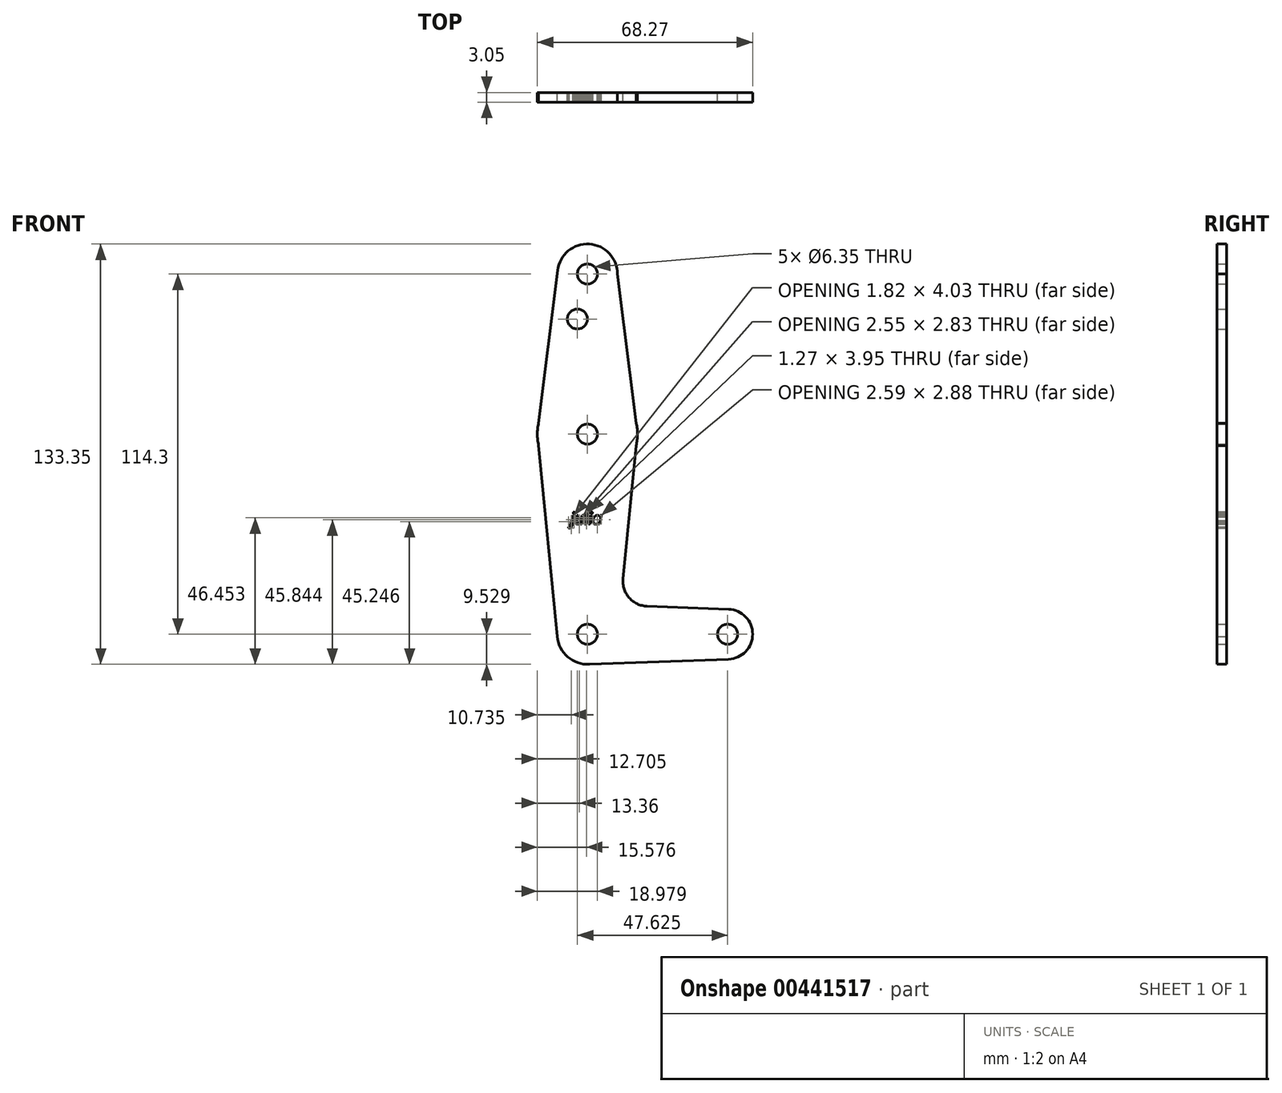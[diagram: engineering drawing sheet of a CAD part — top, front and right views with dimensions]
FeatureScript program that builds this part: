
annotation { "Feature Type Name" : "Feature", "Feature Type Description" : "" }
export const myFeature = defineFeature(function(context is Context, id is Id, definition is map)
    precondition{}
    {
        {
            var Q0;
            Q0=qCreatedBy(makeId("Front.planeOp"),FACE);
            var sketch = newSketch(context, id + "F0", { "sketchPlane" : qUnion([Q0])});
            skLineSegment(sketch, "E0", {"start": v(0, 0) * mm, "end": v(44.45, 0) * mm, "construction": true});
            skCircle(sketch, "E1", {"center": v(0, 114.3) * mm, "radius": 9.53 * mm});
            skCircle(sketch, "E2", {"center": v(0, 0) * mm, "radius": 9.53 * mm});
            skCircle(sketch, "E3", {"center": v(44.45, 0) * mm, "radius": 7.94 * mm});
            skCircle(sketch, "E4", {"center": v(0, 63.5) * mm, "radius": 15.88 * mm});
            skLineSegment(sketch, "E5", {"start": v(0, 114.3) * mm, "end": v(0, 63.5) * mm, "construction": true});
            skLineSegment(sketch, "E6", {"start": v(0, 0) * mm, "end": v(0, 63.5) * mm, "construction": true});
            skLineSegment(sketch, "E7", {"start": v(-15.87, 63.9) * mm, "end": v(-9.45, 115.47) * mm});
            skLineSegment(sketch, "E8", {"start": v(-15.87, 63.9) * mm, "end": v(-9.45, -1.18) * mm});
            skLineSegment(sketch, "E9", {"start": v(9.53, 114.3) * mm, "end": v(15.87, 64.03) * mm});
            skLineSegment(sketch, "E10", {"start": v(15.87, 64.03) * mm, "end": v(11.3, 17.6) * mm});
            skLineSegment(sketch, "E11", {"start": v(18.92, 8.87) * mm, "end": v(44.74, 7.93) * mm});
            skLineSegment(sketch, "E12", {"start": v(0, -9.53) * mm, "end": v(44.73, -7.93) * mm});
            skCircle(sketch, "E13", {"center": v(0, 114.3) * mm, "radius": 3.18 * mm});
            skCircle(sketch, "E14", {"center": v(0, 63.5) * mm, "radius": 3.18 * mm});
            skCircle(sketch, "E15", {"center": v(0, 0) * mm, "radius": 3.18 * mm});
            skCircle(sketch, "E16", {"center": v(44.45, 0) * mm, "radius": 3.18 * mm});
            skCircle(sketch, "E17", {"center": v(-3.18, 100.02) * mm, "radius": 3.18 * mm});
            skPoint(sketch, "E18.newPointB", {"position": v(0, 9.57) * mm});
            skArc(sketch, "E18.filletArc", {"start": v(11.3, 17.6) * mm, "mid": v(13.23, 11.59) * mm, "end": v(18.92, 8.87) * mm});
            skText(sketch, "E19", { "text": "julia", "fontName": "OpenSans-Italic.ttf"});
            const initialGuessF0  = {"E19": [-0.0054, 0.03495, 1, 0, 0.00374]};
            skSetInitialGuess(sketch, initialGuessF0);
            skSolve(sketch);
        }
        {
            var Q0;
            Q0 = qSketchRegion(id + "F0", true);
            extrude(context, id + "F1", {"entities" : qUnion([Q0]), "depth" : 3.05 * mm});
        }
        {
            var Q0;
            Q0 = qSketchRegion(id + "F0", true);
            extrude(context, id + "F2", {"entities" : qUnion([Q0]), "operationType" : NewBodyOperationType.ADD, "depth" : 3.05 * mm});
        }
    });
